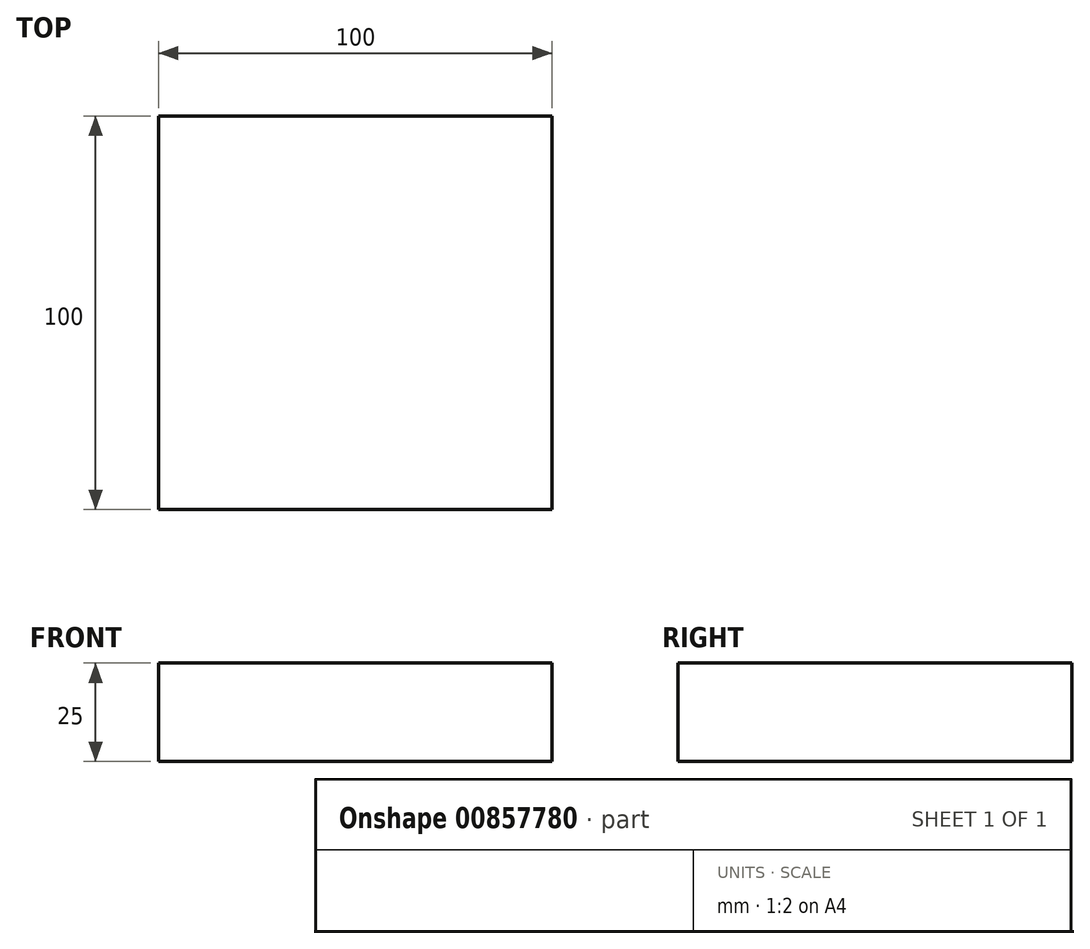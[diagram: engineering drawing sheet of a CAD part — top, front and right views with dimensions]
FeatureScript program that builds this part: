
annotation { "Feature Type Name" : "Feature", "Feature Type Description" : "" }
export const myFeature = defineFeature(function(context is Context, id is Id, definition is map)
    precondition{}
    {
        {
            var Q0;
            Q0=qCreatedBy(makeId("Top.planeOp"),FACE);
            var sketch = newSketch(context, id + "F0", { "sketchPlane" : qUnion([Q0])});
            skLineSegment(sketch, "E0.bottom", {"start": v(0, 0) * mm, "end": v(100, 0) * mm});
            skLineSegment(sketch, "E0.top", {"start": v(0, 100) * mm, "end": v(100, 100) * mm});
            skLineSegment(sketch, "E0.left", {"start": v(0, 0) * mm, "end": v(0, 100) * mm});
            skLineSegment(sketch, "E0.right", {"start": v(100, 0) * mm, "end": v(100, 100) * mm});
            skSolve(sketch);
        }
        {
            var Q0;
            Q0 = qSketchRegion(id + "F0", true);
            extrude(context, id + "F1", {"entities" : qUnion([Q0]), "depth" : 25 * mm, "offsetDistance" : 25 * mm});
        }
    });
